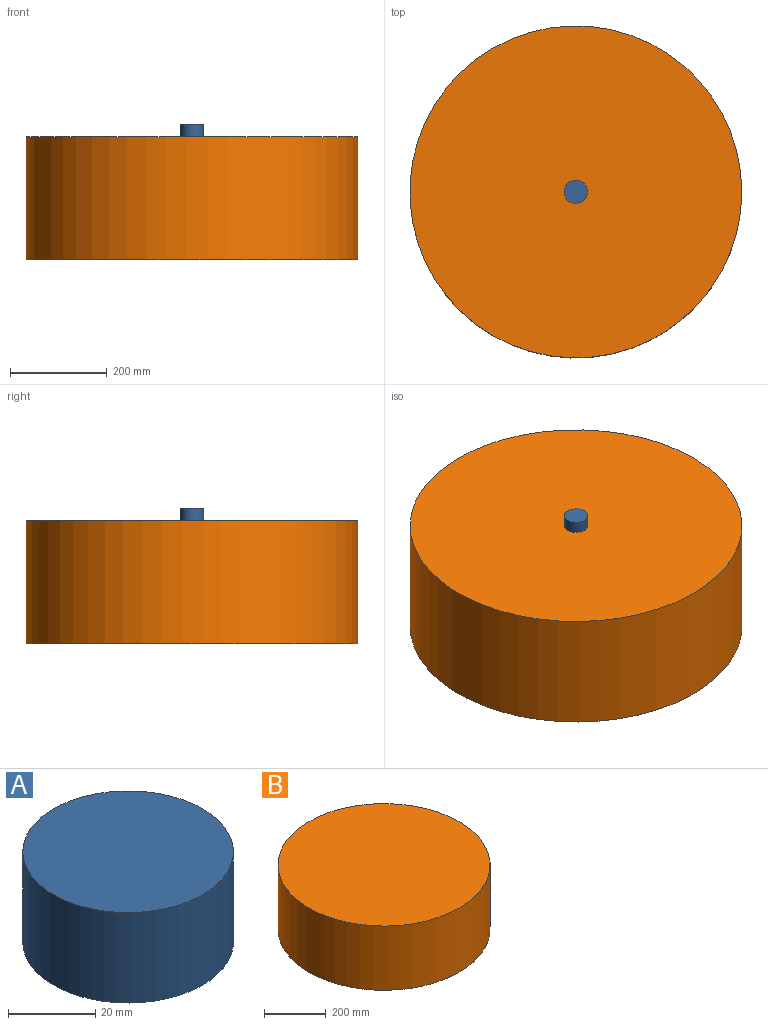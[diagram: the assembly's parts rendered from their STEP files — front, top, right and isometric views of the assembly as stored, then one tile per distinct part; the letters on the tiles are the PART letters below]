
ASSEMBLY  parts=2 mates=1
PART A: 3 faces, bbox 48.3x48.3x25.4 mm
  f0: cylinder r=24.15mm len=48.31mm, axis (0,0,-1), area 3854.8mm2, adj f1,f2
  f1: plane 48.31x48.31mm, normal (0,0,1), area 1832.9mm2, adj f0
  f2: plane 48.31x48.31mm, normal (0,0,-1), area 1832.9mm2, adj f0
PART B: 3 faces, bbox 685.1x685.1x254 mm
  f0: cylinder r=342.53mm len=685.05mm, axis (0,0,-1), area 546646mm2, adj f1,f2
  f1: plane 685.05x685.05mm, normal (0,0,1), area 368582.7mm2, adj f0
  f2: plane 685.05x685.05mm, normal (0,0,-1), area 368582.7mm2, adj f0
PLACE A t=(-36.21,35.08,-43.03)mm
PLACE B t=(278.44,-100.27,-297.03)mm
MATE fastened B.f0 <-> A.f0  axis (0,0,1) through (-36.21,35.08,-43.03)mm
